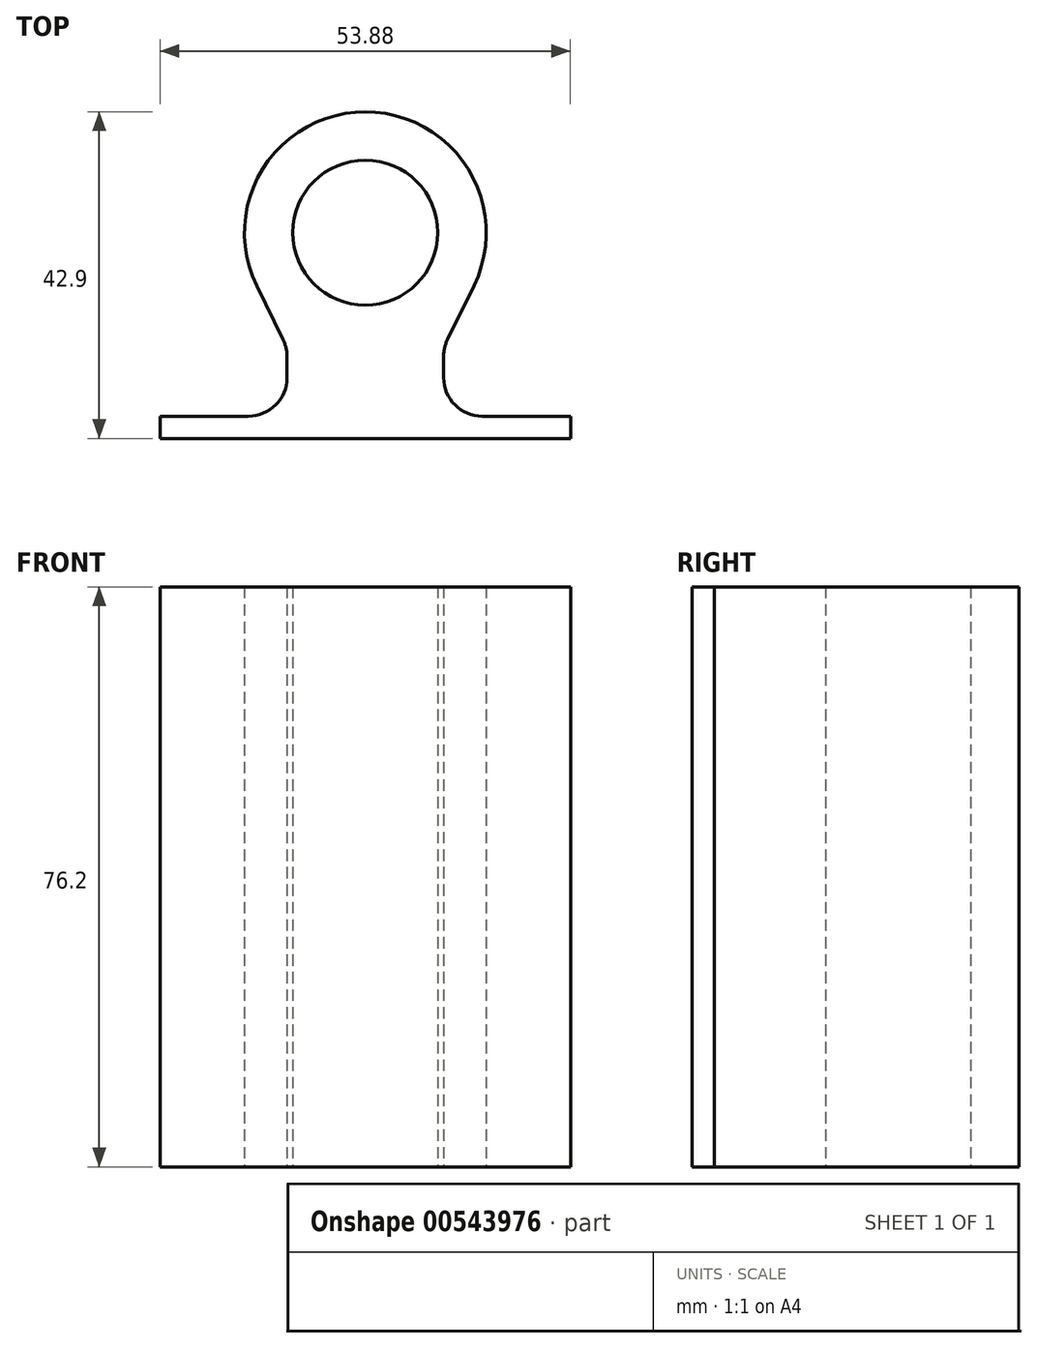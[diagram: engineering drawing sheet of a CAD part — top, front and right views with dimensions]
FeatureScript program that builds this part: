
annotation { "Feature Type Name" : "Feature", "Feature Type Description" : "" }
export const myFeature = defineFeature(function(context is Context, id is Id, definition is map)
    precondition{}
    {
        {
            var Q0;
            Q0=qCreatedBy(makeId("Top.planeOp"),FACE);
            var sketch = newSketch(context, id + "F0", { "sketchPlane" : qUnion([Q0])});
            skCircle(sketch, "E0", {"center": v(0, 0) * mm, "radius": 9.53 * mm});
            skCircle(sketch, "E1.0", {"center": v(0, 0) * mm, "radius": 15.87 * mm});
            skLineSegment(sketch, "E2", {"start": v(14.26, -6.97) * mm, "end": v(10.8, -14.06) * mm});
            skLineSegment(sketch, "E3", {"start": v(-14.26, -6.97) * mm, "end": v(-10.8, -14.06) * mm});
            skLineSegment(sketch, "E4", {"start": v(-10.28, -16.3) * mm, "end": v(-10.28, -19.04) * mm});
            skLineSegment(sketch, "E5", {"start": v(10.28, -16.3) * mm, "end": v(10.28, -19.04) * mm});
            skLineSegment(sketch, "E6", {"start": v(15.36, -24.12) * mm, "end": v(26.94, -24.12) * mm});
            skLineSegment(sketch, "E7", {"start": v(26.94, -24.12) * mm, "end": v(26.94, -27.03) * mm});
            skLineSegment(sketch, "E8", {"start": v(26.94, -27.03) * mm, "end": v(-26.94, -27.03) * mm});
            skLineSegment(sketch, "E9", {"start": v(-26.94, -27.03) * mm, "end": v(-26.94, -24.12) * mm});
            skLineSegment(sketch, "E10", {"start": v(-26.94, -24.12) * mm, "end": v(-15.36, -24.12) * mm});
            skPoint(sketch, "E11", {"position": v(0, -27.03) * mm});
            skLineSegment(sketch, "E12", {"start": v(0, -27.03) * mm, "end": v(0, 0) * mm, "construction": true});
            skPoint(sketch, "E13.visualSharp", {"position": v(-10.28, -15.12) * mm});
            skArc(sketch, "E13.filletArc", {"start": v(-10.28, -16.3) * mm, "mid": v(-10.41, -15.15) * mm, "end": v(-10.8, -14.06) * mm});
            skPoint(sketch, "E14.visualSharp", {"position": v(10.28, -15.12) * mm});
            skArc(sketch, "E14.filletArc", {"start": v(10.8, -14.06) * mm, "mid": v(10.41, -15.15) * mm, "end": v(10.28, -16.3) * mm});
            skPoint(sketch, "E15.visualSharp", {"position": v(10.28, -24.12) * mm});
            skArc(sketch, "E15.filletArc", {"start": v(10.28, -19.04) * mm, "mid": v(11.77, -22.64) * mm, "end": v(15.36, -24.12) * mm});
            skPoint(sketch, "E16.visualSharp", {"position": v(-10.28, -24.12) * mm});
            skArc(sketch, "E16.filletArc", {"start": v(-15.36, -24.12) * mm, "mid": v(-11.77, -22.64) * mm, "end": v(-10.28, -19.04) * mm});
            skLineSegment(sketch, "E17", {"start": v(-10.28, -19.04) * mm, "end": v(0, -19.04) * mm, "construction": true});
            skLineSegment(sketch, "E18", {"start": v(0, -19.04) * mm, "end": v(10.28, -19.04) * mm, "construction": true});
            skSolve(sketch);
        }
        {
            var Q0;
            {var subQ0=sQuery(id+"F0.wireOp",EDGE,"E2");Q0=makeQuery(id+"F0.imprint","IMPRINT",FACE,{"disambiguationData":[TD([[makeQuery(id+"F0.imprint","IMPRINT",EDGE,{"derivedFrom":subQ0}),-1.0]])]});}
            var Q1;
            Q1=makeQuery(id+"F0.imprint","IMPRINT",FACE,{"disambiguationData":[TD([[makeQuery(id+"F0.imprint","IMPRINT",EDGE,{"derivedFrom":sQuery(id+"F0.wireOp",EDGE,"E0")}),-1.0]])]});
            extrude(context, id + "F1", {"entities" : qUnion([Q0, Q1]), "depth" : 76.2 * mm, "offsetDistance" : 25.4 * mm});
        }
    });
